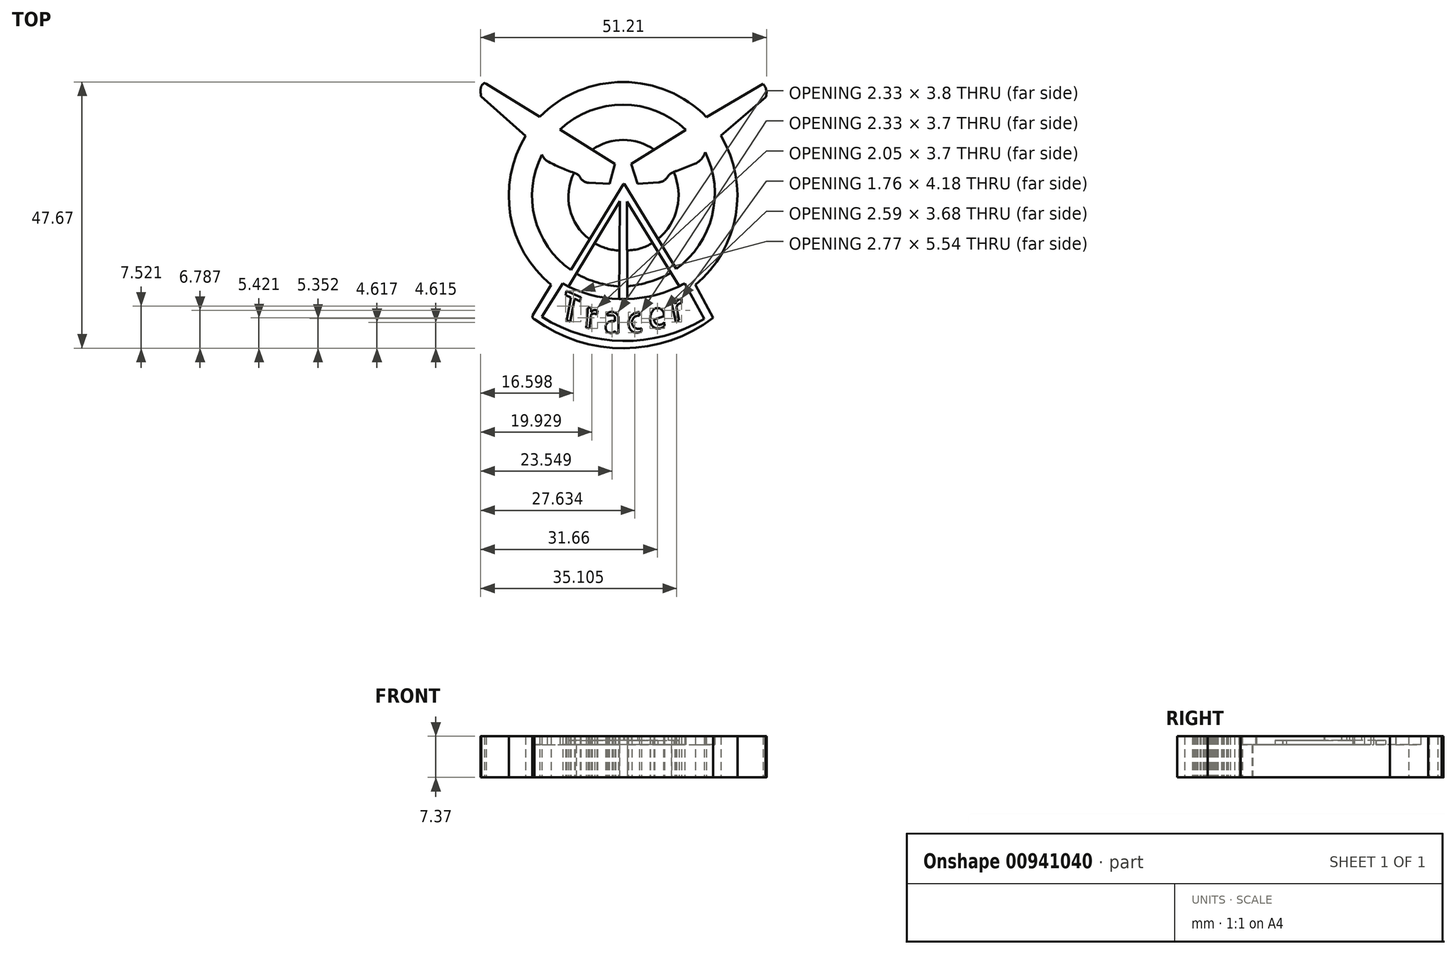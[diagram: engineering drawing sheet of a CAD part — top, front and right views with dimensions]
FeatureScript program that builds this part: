
annotation { "Feature Type Name" : "Feature", "Feature Type Description" : "" }
export const myFeature = defineFeature(function(context is Context, id is Id, definition is map)
    precondition{}
    {
        {
            var Q0;
            Q0=qCreatedBy(makeId("Top.planeOp"),FACE);
            var sketch = newSketch(context, id + "F0", { "sketchPlane" : qUnion([Q0])});
            skArc(sketch, "E0", {"start": v(-8.09, 7.49) * mm, "mid": v(-10.82, -6.71) * mm, "end": v(-3.53, -19.2) * mm});
            skArc(sketch, "E1", {"start": v(24.3, 10.88) * mm, "mid": v(9.37, 17.13) * mm, "end": v(-5.57, 10.9) * mm});
            skArc(sketch, "E2", {"start": v(22.27, -19.2) * mm, "mid": v(29.53, -6.7) * mm, "end": v(26.89, 7.53) * mm});
            skLineSegment(sketch, "E3", {"start": v(-3.53, -19.2) * mm, "end": v(-6.82, -24.67) * mm});
            skArc(sketch, "E4", {"start": v(-6.82, -24.67) * mm, "mid": v(-6.84, -25.08) * mm, "end": v(-6.52, -25.33) * mm});
            skArc(sketch, "E5", {"start": v(-6.52, -25.33) * mm, "mid": v(9.53, -30.54) * mm, "end": v(25.5, -25.09) * mm});
            skLineSegment(sketch, "E6", {"start": v(22.27, -19.2) * mm, "end": v(25.5, -25.09) * mm});
            skLineSegment(sketch, "E7", {"start": v(26.89, 7.53) * mm, "end": v(34.88, 14.39) * mm});
            skArc(sketch, "E8", {"start": v(34.88, 14.39) * mm, "mid": v(35, 15.67) * mm, "end": v(34.4, 16.8) * mm});
            skLineSegment(sketch, "E9", {"start": v(34.4, 16.8) * mm, "end": v(24.3, 10.88) * mm});
            skLineSegment(sketch, "E10", {"start": v(-5.57, 10.9) * mm, "end": v(-15.16, 16.8) * mm});
            skLineSegment(sketch, "E11", {"start": v(-15.16, 16.8) * mm, "end": v(-15.47, 16.97) * mm});
            skArc(sketch, "E12", {"start": v(-15.47, 16.97) * mm, "mid": v(-15.9, 16.62) * mm, "end": v(-16.14, 16.11) * mm});
            skArc(sketch, "E13", {"start": v(-16.14, 16.11) * mm, "mid": v(-16.16, 15.33) * mm, "end": v(-16.07, 14.56) * mm});
            skLineSegment(sketch, "E14", {"start": v(-16.07, 14.56) * mm, "end": v(-8.09, 7.49) * mm});
            skLineSegment(sketch, "E15", {"start": v(-0.83, -20.25) * mm, "end": v(1.81, -21.42) * mm});
            skLineSegment(sketch, "E16", {"start": v(1.81, -21.42) * mm, "end": v(1.68, -22.17) * mm});
            skLineSegment(sketch, "E17", {"start": v(1.68, -22.17) * mm, "end": v(0.74, -21.74) * mm});
            skLineSegment(sketch, "E18", {"start": v(0.74, -21.74) * mm, "end": v(0.65, -21.71) * mm});
            skLineSegment(sketch, "E19", {"start": v(0.65, -21.71) * mm, "end": v(-0.09, -25.8) * mm});
            skLineSegment(sketch, "E20", {"start": v(-0.09, -25.8) * mm, "end": v(-0.74, -25.52) * mm});
            skLineSegment(sketch, "E21", {"start": v(-0.74, -25.52) * mm, "end": v(0, -21.46) * mm});
            skLineSegment(sketch, "E22", {"start": v(0, -21.46) * mm, "end": v(-0.96, -21.02) * mm});
            skLineSegment(sketch, "E23", {"start": v(-0.96, -21.02) * mm, "end": v(-0.83, -20.25) * mm});
            skLineSegment(sketch, "E24", {"start": v(3.03, -23.27) * mm, "end": v(3.61, -23.3) * mm});
            skLineSegment(sketch, "E25", {"start": v(3.61, -23.3) * mm, "end": v(3.61, -23.98) * mm});
            skArc(sketch, "E26", {"start": v(4.3, -23.7) * mm, "mid": v(4, -23.75) * mm, "end": v(3.8, -23.98) * mm});
            skArc(sketch, "E27", {"start": v(4.78, -23.86) * mm, "mid": v(4.55, -23.74) * mm, "end": v(4.3, -23.7) * mm});
            skLineSegment(sketch, "E28", {"start": v(4.78, -23.86) * mm, "end": v(4.65, -24.52) * mm});
            skArc(sketch, "E29", {"start": v(4.65, -24.52) * mm, "mid": v(4.13, -24.36) * mm, "end": v(3.6, -24.52) * mm});
            skLineSegment(sketch, "E30", {"start": v(3.6, -24.52) * mm, "end": v(3.3, -26.97) * mm});
            skLineSegment(sketch, "E31", {"start": v(3.3, -26.97) * mm, "end": v(2.74, -26.86) * mm});
            skLineSegment(sketch, "E32", {"start": v(2.74, -26.86) * mm, "end": v(3.03, -23.27) * mm});
            skArc(sketch, "E33", {"start": v(8.54, -25.09) * mm, "mid": v(7.8, -24.13) * mm, "end": v(6.6, -24.23) * mm});
            skLineSegment(sketch, "E34", {"start": v(8.54, -25.09) * mm, "end": v(8.54, -27.69) * mm});
            skArc(sketch, "E35", {"start": v(8.4, -27.82) * mm, "mid": v(8.5, -27.78) * mm, "end": v(8.54, -27.69) * mm});
            skLineSegment(sketch, "E36", {"start": v(8.4, -27.82) * mm, "end": v(8, -27.82) * mm});
            skLineSegment(sketch, "E37", {"start": v(8, -27.82) * mm, "end": v(8, -27.58) * mm});
            skArc(sketch, "E38", {"start": v(8, -27.58) * mm, "mid": v(7.78, -27.57) * mm, "end": v(7.6, -27.7) * mm});
            skArc(sketch, "E39", {"start": v(6.89, -27.76) * mm, "mid": v(7.25, -27.8) * mm, "end": v(7.6, -27.7) * mm});
            skArc(sketch, "E40", {"start": v(6.32, -27.24) * mm, "mid": v(6.53, -27.58) * mm, "end": v(6.89, -27.76) * mm});
            skArc(sketch, "E41", {"start": v(6.64, -25.95) * mm, "mid": v(6.24, -26.54) * mm, "end": v(6.32, -27.24) * mm});
            skArc(sketch, "E42", {"start": v(7.86, -25.7) * mm, "mid": v(7.22, -25.69) * mm, "end": v(6.64, -25.95) * mm});
            skArc(sketch, "E43", {"start": v(7.86, -25.7) * mm, "mid": v(7.9, -25.6) * mm, "end": v(7.91, -25.51) * mm});
            skLineSegment(sketch, "E44", {"start": v(7.91, -25.51) * mm, "end": v(7.87, -24.95) * mm});
            skArc(sketch, "E45", {"start": v(7.87, -24.95) * mm, "mid": v(7.68, -24.73) * mm, "end": v(7.4, -24.64) * mm});
            skArc(sketch, "E46", {"start": v(7.4, -24.64) * mm, "mid": v(7, -24.64) * mm, "end": v(6.6, -24.67) * mm});
            skArc(sketch, "E47", {"start": v(6.49, -24.64) * mm, "mid": v(6.54, -24.68) * mm, "end": v(6.6, -24.67) * mm});
            skArc(sketch, "E48", {"start": v(6.6, -24.23) * mm, "mid": v(6.5, -24.42) * mm, "end": v(6.49, -24.64) * mm});
            skArc(sketch, "E49", {"start": v(12.25, -24.07) * mm, "mid": v(10.56, -25.08) * mm, "end": v(10.57, -27.06) * mm});
            skArc(sketch, "E50", {"start": v(10.57, -27.06) * mm, "mid": v(11.5, -27.74) * mm, "end": v(12.63, -27.5) * mm});
            skLineSegment(sketch, "E51", {"start": v(12.63, -27.5) * mm, "end": v(12.63, -26.96) * mm});
            skArc(sketch, "E52", {"start": v(12.25, -24.72) * mm, "mid": v(10.95, -26.1) * mm, "end": v(12.63, -26.96) * mm});
            skLineSegment(sketch, "E53", {"start": v(12.25, -24.07) * mm, "end": v(12.25, -24.72) * mm});
            skLineSegment(sketch, "E54", {"start": v(16.6, -24.85) * mm, "end": v(14.9, -25.42) * mm});
            skArc(sketch, "E55", {"start": v(14.9, -25.42) * mm, "mid": v(15.65, -26.31) * mm, "end": v(16.73, -25.87) * mm});
            skLineSegment(sketch, "E56", {"start": v(16.73, -25.87) * mm, "end": v(16.79, -26.5) * mm});
            skArc(sketch, "E57", {"start": v(14.2, -25.6) * mm, "mid": v(15.18, -26.94) * mm, "end": v(16.79, -26.5) * mm});
            skArc(sketch, "E58", {"start": v(14.97, -23.47) * mm, "mid": v(14.34, -24.44) * mm, "end": v(14.2, -25.6) * mm});
            skArc(sketch, "E59", {"start": v(16.6, -24.85) * mm, "mid": v(16.24, -23.61) * mm, "end": v(14.97, -23.47) * mm});
            skArc(sketch, "E60", {"start": v(15.89, -24.54) * mm, "mid": v(15.19, -24.07) * mm, "end": v(14.86, -24.85) * mm});
            skLineSegment(sketch, "E61", {"start": v(15.9, -24.54) * mm, "end": v(14.86, -24.85) * mm});
            skLineSegment(sketch, "E62", {"start": v(18.05, -22.47) * mm, "end": v(18.59, -22.17) * mm});
            skLineSegment(sketch, "E63", {"start": v(18.59, -22.17) * mm, "end": v(18.74, -22.61) * mm});
            skArc(sketch, "E64", {"start": v(19.8, -21.66) * mm, "mid": v(19.13, -21.97) * mm, "end": v(18.74, -22.6) * mm});
            skLineSegment(sketch, "E65", {"start": v(19.8, -21.66) * mm, "end": v(19.82, -22.45) * mm});
            skArc(sketch, "E66", {"start": v(19.82, -22.45) * mm, "mid": v(19.21, -22.7) * mm, "end": v(18.91, -23.3) * mm});
            skLineSegment(sketch, "E67", {"start": v(18.91, -23.3) * mm, "end": v(19.38, -25.55) * mm});
            skLineSegment(sketch, "E68", {"start": v(19.38, -25.55) * mm, "end": v(18.78, -25.84) * mm});
            skLineSegment(sketch, "E69", {"start": v(18.78, -25.84) * mm, "end": v(18.05, -22.47) * mm});
            skLineSegment(sketch, "E70", {"start": v(-5.57, 10.9) * mm, "end": v(7.92, 2.45) * mm});
            skLineSegment(sketch, "E71", {"start": v(7.92, 2.45) * mm, "end": v(6.91, -1.08) * mm});
            skLineSegment(sketch, "E72", {"start": v(6.91, -1.08) * mm, "end": v(3.24, -0.9) * mm});
            skArc(sketch, "E73", {"start": v(1.77, -0.2) * mm, "mid": v(2.43, -0.7) * mm, "end": v(3.24, -0.9) * mm});
            skArc(sketch, "E74", {"start": v(1.77, -0.2) * mm, "mid": v(1.3, 0.49) * mm, "end": v(0.57, 0.87) * mm});
            skArc(sketch, "E75", {"start": v(-4.25, 2.98) * mm, "mid": v(-1.9, 1.82) * mm, "end": v(0.57, 0.87) * mm});
            skArc(sketch, "E76", {"start": v(-5.3, 4.57) * mm, "mid": v(-4.93, 3.67) * mm, "end": v(-4.25, 2.98) * mm});
            skArc(sketch, "E77", {"start": v(-5.3, 4.57) * mm, "mid": v(-5.45, 5.18) * mm, "end": v(-5.88, 5.65) * mm});
            skLineSegment(sketch, "E78", {"start": v(-8.09, 7.49) * mm, "end": v(-5.88, 5.65) * mm});
            skLineSegment(sketch, "E79", {"start": v(24.3, 10.88) * mm, "end": v(10.82, 2.47) * mm});
            skLineSegment(sketch, "E80", {"start": v(10.82, 2.47) * mm, "end": v(11.96, -1.07) * mm});
            skLineSegment(sketch, "E81", {"start": v(11.96, -1.07) * mm, "end": v(15.7, -0.83) * mm});
            skArc(sketch, "E82", {"start": v(15.7, -0.83) * mm, "mid": v(16.7, -0.5) * mm, "end": v(17.4, 0.3) * mm});
            skArc(sketch, "E83", {"start": v(18.9, 1.2) * mm, "mid": v(18.1, 0.85) * mm, "end": v(17.4, 0.3) * mm});
            skLineSegment(sketch, "E84", {"start": v(18.9, 1.2) * mm, "end": v(22.14, 2.47) * mm});
            skArc(sketch, "E85", {"start": v(22.14, 2.47) * mm, "mid": v(23.35, 3.3) * mm, "end": v(24.07, 4.58) * mm});
            skArc(sketch, "E86", {"start": v(24.67, 5.62) * mm, "mid": v(24.26, 5.16) * mm, "end": v(24.07, 4.58) * mm});
            skLineSegment(sketch, "E87", {"start": v(26.89, 7.53) * mm, "end": v(24.67, 5.62) * mm});
            skArc(sketch, "E88", {"start": v(20.6, 8.57) * mm, "mid": v(9.34, 13.09) * mm, "end": v(-1.93, 8.63) * mm});
            skArc(sketch, "E89", {"start": v(-5.17, 4.14) * mm, "mid": v(-6.47, -7.17) * mm, "end": v(0, -16.54) * mm});
            skLineSegment(sketch, "E90", {"start": v(0, -16.54) * mm, "end": v(-1.48, -18.91) * mm});
            skLineSegment(sketch, "E91", {"start": v(-1.48, -18.91) * mm, "end": v(-0.42, -19.52) * mm});
            skLineSegment(sketch, "E92", {"start": v(-0.42, -19.52) * mm, "end": v(8.8, -4.17) * mm});
            skLineSegment(sketch, "E93", {"start": v(8.8, -4.17) * mm, "end": v(8.66, -21.72) * mm});
            skLineSegment(sketch, "E94", {"start": v(8.66, -21.72) * mm, "end": v(10.11, -21.73) * mm});
            skLineSegment(sketch, "E95", {"start": v(10.11, -21.73) * mm, "end": v(10.02, -4.29) * mm});
            skLineSegment(sketch, "E96", {"start": v(10.02, -4.29) * mm, "end": v(19.4, -19.35) * mm});
            skLineSegment(sketch, "E97", {"start": v(19.4, -19.35) * mm, "end": v(20.4, -18.91) * mm});
            skLineSegment(sketch, "E98", {"start": v(20.4, -18.91) * mm, "end": v(9.58, -1.14) * mm});
            skLineSegment(sketch, "E99", {"start": v(9.58, -1.14) * mm, "end": v(9.51, -1.08) * mm});
            skLineSegment(sketch, "E100", {"start": v(9.51, -1.08) * mm, "end": v(9.4, -1.14) * mm});
            skLineSegment(sketch, "E101", {"start": v(9.4, -1.14) * mm, "end": v(0, -16.54) * mm});
            skArc(sketch, "E102", {"start": v(-0.42, -19.52) * mm, "mid": v(10.07, -21.73) * mm, "end": v(20.4, -18.91) * mm});
            skLineSegment(sketch, "E103", {"start": v(20.4, -18.91) * mm, "end": v(23.88, -25.3) * mm});
            skArc(sketch, "E104", {"start": v(-5.2, -24.9) * mm, "mid": v(9.28, -29.24) * mm, "end": v(23.88, -25.3) * mm});
            skLineSegment(sketch, "E105", {"start": v(-1.48, -18.91) * mm, "end": v(-5.2, -24.9) * mm});
            skArc(sketch, "E106", {"start": v(0.99, -17.18) * mm, "mid": v(4.7, -18.77) * mm, "end": v(8.68, -19.47) * mm});
            skArc(sketch, "E107", {"start": v(10.1, -19.47) * mm, "mid": v(14.15, -18.63) * mm, "end": v(17.96, -17.04) * mm});
            skArc(sketch, "E108", {"start": v(18.85, -16.35) * mm, "mid": v(25.28, -6.84) * mm, "end": v(24.07, 4.58) * mm});
            skArc(sketch, "E109", {"start": v(15.6, -11) * mm, "mid": v(19.02, -5.47) * mm, "end": v(18.4, 1.02) * mm});
            skArc(sketch, "E110", {"start": v(10.07, -13) * mm, "mid": v(12.44, -12.67) * mm, "end": v(14.61, -11.67) * mm});
            skArc(sketch, "E111", {"start": v(4.26, -11.72) * mm, "mid": v(6.41, -12.66) * mm, "end": v(8.73, -13.06) * mm});
            skArc(sketch, "E112", {"start": v(0.57, 0.87) * mm, "mid": v(-0.2, -5.59) * mm, "end": v(3.37, -11.02) * mm});
            skArc(sketch, "E113", {"start": v(14.93, 5.04) * mm, "mid": v(9.38, 6.76) * mm, "end": v(3.83, 5.01) * mm});
            skArc(sketch, "E114", {"start": v(3.61, -23.98) * mm, "mid": v(3.7, -24.02) * mm, "end": v(3.8, -23.98) * mm});
            skArc(sketch, "E115", {"start": v(18.74, -22.6) * mm, "mid": v(18.74, -22.6) * mm, "end": v(18.74, -22.61) * mm});
            skSolve(sketch);
        }
        {
            var Q0;
            Q0 = qSketchRegion(id + "F0", true);
            var Q1;
            {var subQ24=sQuery(id+"F0.wireOp",EDGE,"E90");Q1=makeQuery(id+"F0.imprint","IMPRINT",FACE,{"disambiguationData":[TD([[makeQuery(id+"F0.imprint","IMPRINT",EDGE,{"derivedFrom":subQ24}),1.0]])]});}
            extrude(context, id + "F1", {"entities" : qUnion([Q0, Q1]), "depth" : 7.37 * mm, "offsetDistance" : 25.4 * mm});
        }
        {
            var Q0;
            Q0=makeQuery(id+"F0.imprint","IMPRINT",FACE,{"disambiguationData":[TD([[makeQuery(id+"F0.imprint","IMPRINT",EDGE,{"derivedFrom":sQuery(id+"F0.wireOp",EDGE,"E15")}),1.0]])]});
            extrude(context, id + "F2", {"entities" : qUnion([Q0]), "depth" : 7.37 * mm, "offsetDistance" : 25.4 * mm});
        }
        {
            var Q0;
            {var subQ3=sQuery(id+"F0.wireOp",EDGE,"E111");Q0=makeQuery(id+"F0.imprint","IMPRINT",FACE,{"disambiguationData":[TD([[makeQuery(id+"F0.imprint","IMPRINT",EDGE,{"derivedFrom":subQ3}),1.0]])]});}
            var Q1;
            {var subQ3=sQuery(id+"F0.wireOp",EDGE,"E110");Q1=makeQuery(id+"F0.imprint","IMPRINT",FACE,{"disambiguationData":[TD([[makeQuery(id+"F0.imprint","IMPRINT",EDGE,{"derivedFrom":subQ3}),1.0]])]});}
            var Q2;
            {var subQ3=sQuery(id+"F0.wireOp",EDGE,"E71");Q2=makeQuery(id+"F0.imprint","IMPRINT",FACE,{"disambiguationData":[TD([[makeQuery(id+"F0.imprint","IMPRINT",EDGE,{"derivedFrom":subQ3}),1.0]])]});}
            extrude(context, id + "F3", {"entities" : qUnion([Q0, Q1, Q2]), "operationType" : NewBodyOperationType.ADD, "depth" : 6.6 * mm, "offsetDistance" : 25.4 * mm});
        }
        {
            var Q0;
            {var subQ0=sQuery(id+"F0.wireOp",EDGE,"E107");Q0=makeQuery(id+"F0.imprint","IMPRINT",FACE,{"disambiguationData":[TD([[makeQuery(id+"F0.imprint","IMPRINT",EDGE,{"derivedFrom":subQ0}),1.0]])]});}
            var Q1;
            {var subQ0=sQuery(id+"F0.wireOp",EDGE,"E106");Q1=makeQuery(id+"F0.imprint","IMPRINT",FACE,{"disambiguationData":[TD([[makeQuery(id+"F0.imprint","IMPRINT",EDGE,{"derivedFrom":subQ0}),1.0]])]});}
            var Q2;
            {var subQ3=sQuery(id+"F0.wireOp",EDGE,"E84");Q2=makeQuery(id+"F0.imprint","IMPRINT",FACE,{"disambiguationData":[TD([[makeQuery(id+"F0.imprint","IMPRINT",EDGE,{"derivedFrom":subQ3}),-1.0]])]});}
            var Q3;
            {var subQ4=sQuery(id+"F0.wireOp",EDGE,"E75");Q3=makeQuery(id+"F0.imprint","IMPRINT",FACE,{"disambiguationData":[TD([[makeQuery(id+"F0.imprint","IMPRINT",EDGE,{"derivedFrom":subQ4}),-1.0]])]});}
            var Q4;
            {var subQ0=sQuery(id+"F0.wireOp",EDGE,"E88");Q4=makeQuery(id+"F0.imprint","IMPRINT",FACE,{"disambiguationData":[TD([[makeQuery(id+"F0.imprint","IMPRINT",EDGE,{"derivedFrom":subQ0}),1.0]])]});}
            extrude(context, id + "F4", {"entities" : qUnion([Q0, Q1, Q2, Q3, Q4]), "operationType" : NewBodyOperationType.ADD, "depth" : 5.84 * mm, "offsetDistance" : 25.4 * mm});
        }
    });
